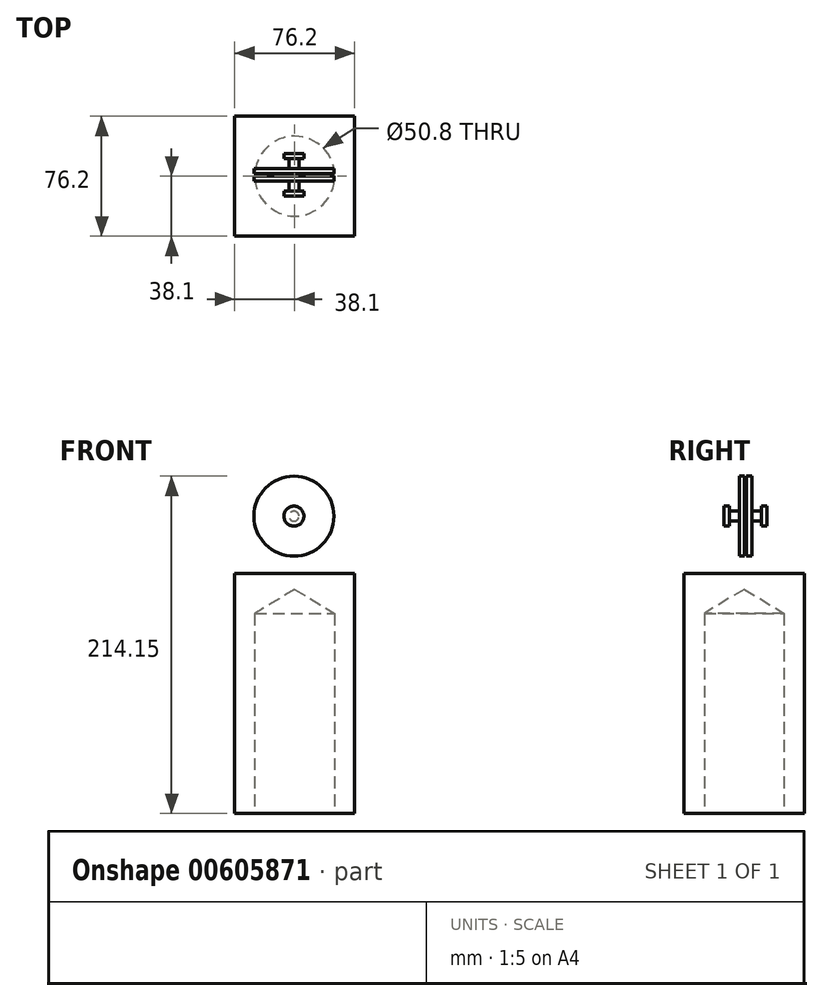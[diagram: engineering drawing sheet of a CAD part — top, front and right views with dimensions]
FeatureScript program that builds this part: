
annotation { "Feature Type Name" : "Feature", "Feature Type Description" : "" }
export const myFeature = defineFeature(function(context is Context, id is Id, definition is map)
    precondition{}
    {
        {
            var Q0;
            Q0=qCreatedBy(makeId("Front.planeOp"),FACE);
            var sketch = newSketch(context, id + "F0", { "sketchPlane" : qUnion([Q0])});
            skLineSegment(sketch, "E0", {"start": v(0, 0) * mm, "end": v(76.2, 0) * mm});
            skLineSegment(sketch, "E1", {"start": v(76.2, 0) * mm, "end": v(76.2, 152.4) * mm});
            skLineSegment(sketch, "E2", {"start": v(76.2, 152.4) * mm, "end": v(0, 152.4) * mm});
            skLineSegment(sketch, "E3", {"start": v(0, 152.4) * mm, "end": v(0, 0) * mm});
            skSolve(sketch);
        }
        {
            var Q0;
            Q0=makeQuery(id+"F0.imprint","IMPRINT",FACE,{"disambiguationData":[TD([[makeQuery(id+"F0.imprint","IMPRINT",EDGE,{"derivedFrom":sQuery(id+"F0.wireOp",EDGE,"E0")}),1.0]])]});
            extrude(context, id + "F1", {"entities" : qUnion([Q0]), "oppositeDirection" : true, "depth" : 76.2 * mm, "offsetDistance" : 25.4 * mm});
        }
        {
            var Q0;
            Q0=makeQuery(id+"F1.opExtrude","SWEPT_FACE",FACE,{"disambiguationData":[OSD([sQuery(id+"F0.wireOp",EDGE,"E0")])]});
            var sketch = newSketch(context, id + "F2", { "sketchPlane" : qUnion([Q0])});
            skLineSegment(sketch, "E4", {"start": v(76.2, -38.1) * mm, "end": v(38.1, -38.1) * mm});
            skPoint(sketch, "E4.endSnap0", {"position": v(76.2, -38.1) * mm});
            skSolve(sketch);
        }
        {
            var Q0;
            Q0=sQuery(id+"F2.wireOp",VERTEX,"E4.end");
            var Q1;
            Q1=makeQuery(id+"F1.opExtrude","SWEPT_BODY",BODY,{"disambiguationData":[OSD([sQuery(id+"F0.wireOp",EDGE,"E0"),sQuery(id+"F0.wireOp",EDGE,"E1"),sQuery(id+"F0.wireOp",EDGE,"E2"),sQuery(id+"F0.wireOp",EDGE,"E3")])]});
            hole(context, id + "F3", {"style" : HoleStyle.SIMPLE, "endStyle" : HoleEndStyle.BLIND, "holeDiameter" : 50.8 * mm, "majorDiameter" : 6.35 * mm, "holeDepth" : 127 * mm, "isTappedThrough" : true, "tappedDepth" : 12.7 * mm, "tapClearance" : 3, "startFromSketch" : true, "locations" : qUnion([Q0]), "scope" : qUnion([Q1])});
        }
        {
            var Q0;
            Q0=qCreatedBy(makeId("Front.planeOp"),FACE);
            cPlane(context, id + "F4", {"entities" : qUnion([Q0]), "cplaneType" : CPlaneType.OFFSET, "offset" : 38.1 * mm, "oppositeDirection" : true, "width" : 152.4 * mm, "height" : 152.4 * mm});
        }
        {
            var Q0;
            Q0=qCreatedBy(id+"F4.planeOp",FACE);
            var sketch = newSketch(context, id + "F5", { "sketchPlane" : qUnion([Q0])});
            skCircle(sketch, "E5", {"center": v(37.63, 188.75) * mm, "radius": 25.4 * mm});
            skSolve(sketch);
        }
        {
            var Q0;
            Q0=makeQuery(id+"F1.opExtrude","CAP_VERTEX",VERTEX,{"disambiguationData":[OSD([sQuery(id+"F0.wireOp",EDGE,"E2"),sQuery(id+"F0.wireOp",EDGE,"E3")])],"isStart":true});
            var Q1;
            Q1=makeQuery(id+"F1.opExtrude","CAP_VERTEX",VERTEX,{"disambiguationData":[OSD([sQuery(id+"F0.wireOp",EDGE,"E1"),sQuery(id+"F0.wireOp",EDGE,"E2")])],"isStart":true});
            var Q2;
            Q2=sQuery(id+"F5.wireOp",VERTEX,"E5.center");
            cPlane(context, id + "F6", {"entities" : qUnion([Q0, Q1, Q2]), "cplaneType" : CPlaneType.THREE_POINT, "offset" : 25.4 * mm, "width" : 152.4 * mm, "height" : 152.4 * mm});
        }
        {
            var Q0;
            Q0=makeQuery(id+"F5.imprint","IMPRINT",FACE,{"disambiguationData":[TD([[makeQuery(id+"F5.imprint","IMPRINT",EDGE,{"derivedFrom":sQuery(id+"F5.wireOp",EDGE,"E5")}),1.0]])]});
            extrude(context, id + "F7", {"entities" : qUnion([Q0]), "depth" : 3.17 * mm, "offsetDistance" : 25.4 * mm});
        }
        {
            var Q0;
            Q0=makeQuery(id+"F7.opExtrude","CAP_FACE",FACE,{"disambiguationData":[OSD([sQuery(id+"F5.wireOp",EDGE,"E5")])],"isStart":true});
            var sketch = newSketch(context, id + "F8", { "sketchPlane" : qUnion([Q0])});
            skCircle(sketch, "E6", {"center": v(-37.63, 188.75) * mm, "radius": 3.18 * mm});
            skSolve(sketch);
        }
        {
            var Q0;
            Q0=makeQuery(id+"F8.imprint","IMPRINT",FACE,{"disambiguationData":[TD([[makeQuery(id+"F8.imprint","IMPRINT",EDGE,{"derivedFrom":sQuery(id+"F8.wireOp",EDGE,"E6")}),1.0]])]});
            var Q1;
            Q1=sQuery(id+"F8.wireOp",EDGE,"E6");
            extrude(context, id + "F9", {"entities" : qUnion([Q0]), "operationType" : NewBodyOperationType.ADD, "surfaceEntities" : qUnion([Q1]), "depth" : 1.59 * mm, "offsetDistance" : 25.4 * mm});
        }
        {
            var Q0;
            Q0=makeQuery(id+"F9.opExtrude","CAP_FACE",FACE,{"disambiguationData":[OSD([sQuery(id+"F8.wireOp",EDGE,"E6")])],"isStart":false});
            var sketch = newSketch(context, id + "F10", { "sketchPlane" : qUnion([Q0])});
            skCircle(sketch, "E7", {"center": v(-37.63, 188.75) * mm, "radius": 25.4 * mm});
            skSolve(sketch);
        }
        {
            var Q0;
            Q0=makeQuery(id+"F10.imprint","IMPRINT",FACE,{"disambiguationData":[TD([[makeQuery(id+"F10.imprint","IMPRINT",EDGE,{"derivedFrom":makeQuery(id+"F9.opExtrude","CAP_EDGE",EDGE,{"disambiguationData":[OSD([sQuery(id+"F8.wireOp",EDGE,"E6")])],"isStart":false})}),1.0]])]});
            extrude(context, id + "F11", {"entities" : qUnion([Q0]), "operationType" : NewBodyOperationType.ADD, "depth" : 3.17 * mm, "offsetDistance" : 25.4 * mm});
        }
        {
            var Q0;
            Q0=makeQuery(id+"F10.imprint","IMPRINT",FACE,{"disambiguationData":[TD([[makeQuery(id+"F10.imprint","IMPRINT",EDGE,{"derivedFrom":sQuery(id+"F10.wireOp",EDGE,"E7")}),1.0]])]});
            extrude(context, id + "F12", {"entities" : qUnion([Q0]), "operationType" : NewBodyOperationType.ADD, "depth" : 3.17 * mm, "offsetDistance" : 25.4 * mm});
        }
        {
            var Q0;
            {var subQ0=sQuery(id+"F8.wireOp",EDGE,"E6");Q0=makeQuery(id+"F12.boolean.opBoolean","MERGE",FACE,{"derivedFrom":[makeQuery(id+"F11.opExtrude","CAP_FACE",FACE,{"disambiguationData":[OSD([subQ0])],"isStart":false}),makeQuery(id+"F12.opExtrude","CAP_FACE",FACE,{"disambiguationData":[OSD([subQ0,sQuery(id+"F10.wireOp",EDGE,"E7")])],"isStart":false})]});}
            var sketch = newSketch(context, id + "F13", { "sketchPlane" : qUnion([Q0])});
            skCircle(sketch, "E8", {"center": v(-37.63, 188.75) * mm, "radius": 3.18 * mm});
            skSolve(sketch);
        }
        {
            var Q0;
            Q0=makeQuery(id+"F13.imprint","IMPRINT",FACE,{"disambiguationData":[TD([[makeQuery(id+"F13.imprint","IMPRINT",EDGE,{"derivedFrom":sQuery(id+"F13.wireOp",EDGE,"E8")}),1.0]])]});
            extrude(context, id + "F14", {"entities" : qUnion([Q0]), "operationType" : NewBodyOperationType.ADD, "depth" : 6.35 * mm, "offsetDistance" : 25.4 * mm});
        }
        {
            var Q0;
            Q0=makeQuery(id+"F7.opExtrude","CAP_FACE",FACE,{"disambiguationData":[OSD([sQuery(id+"F5.wireOp",EDGE,"E5")])],"isStart":false});
            var sketch = newSketch(context, id + "F15", { "sketchPlane" : qUnion([Q0])});
            skCircle(sketch, "E9", {"center": v(37.63, 188.75) * mm, "radius": 3.18 * mm});
            skSolve(sketch);
        }
        {
            var Q0;
            Q0=makeQuery(id+"F15.imprint","IMPRINT",FACE,{"disambiguationData":[TD([[makeQuery(id+"F15.imprint","IMPRINT",EDGE,{"derivedFrom":sQuery(id+"F15.wireOp",EDGE,"E9")}),1.0]])]});
            extrude(context, id + "F16", {"entities" : qUnion([Q0]), "operationType" : NewBodyOperationType.ADD, "depth" : 6.35 * mm, "offsetDistance" : 25.4 * mm});
        }
        {
            var Q0;
            Q0=makeQuery(id+"F16.opExtrude","CAP_FACE",FACE,{"disambiguationData":[OSD([sQuery(id+"F15.wireOp",EDGE,"E9")])],"isStart":false});
            var sketch = newSketch(context, id + "F17", { "sketchPlane" : qUnion([Q0])});
            skCircle(sketch, "E10", {"center": v(37.63, 188.75) * mm, "radius": 6.35 * mm});
            skSolve(sketch);
        }
        {
            var Q0;
            Q0=makeQuery(id+"F17.imprint","IMPRINT",FACE,{"disambiguationData":[TD([[makeQuery(id+"F17.imprint","IMPRINT",EDGE,{"derivedFrom":makeQuery(id+"F16.opExtrude","CAP_EDGE",EDGE,{"disambiguationData":[OSD([sQuery(id+"F15.wireOp",EDGE,"E9")])],"isStart":false})}),1.0]])]});
            extrude(context, id + "F18", {"entities" : qUnion([Q0]), "operationType" : NewBodyOperationType.ADD, "depth" : 3.17 * mm, "offsetDistance" : 25.4 * mm});
        }
        {
            var Q0;
            Q0=makeQuery(id+"F17.imprint","IMPRINT",FACE,{"disambiguationData":[TD([[makeQuery(id+"F17.imprint","IMPRINT",EDGE,{"derivedFrom":sQuery(id+"F17.wireOp",EDGE,"E10")}),1.0]])]});
            extrude(context, id + "F19", {"entities" : qUnion([Q0]), "operationType" : NewBodyOperationType.ADD, "depth" : 3.17 * mm, "offsetDistance" : 25.4 * mm});
        }
        {
            var Q0;
            Q0=makeQuery(id+"F14.opExtrude","CAP_FACE",FACE,{"disambiguationData":[OSD([sQuery(id+"F13.wireOp",EDGE,"E8")])],"isStart":false});
            var sketch = newSketch(context, id + "F20", { "sketchPlane" : qUnion([Q0])});
            skCircle(sketch, "E11", {"center": v(-37.63, 188.75) * mm, "radius": 6.35 * mm});
            skSolve(sketch);
        }
        {
            var Q0;
            Q0=makeQuery(id+"F20.imprint","IMPRINT",FACE,{"disambiguationData":[TD([[makeQuery(id+"F20.imprint","IMPRINT",EDGE,{"derivedFrom":makeQuery(id+"F14.opExtrude","CAP_EDGE",EDGE,{"disambiguationData":[OSD([sQuery(id+"F13.wireOp",EDGE,"E8")])],"isStart":false})}),1.0]])]});
            extrude(context, id + "F21", {"entities" : qUnion([Q0]), "operationType" : NewBodyOperationType.ADD, "depth" : 3.17 * mm, "offsetDistance" : 25.4 * mm});
        }
        {
            var Q0;
            Q0 = qSketchRegion(id + "F20", true);
            extrude(context, id + "F22", {"entities" : qUnion([Q0]), "operationType" : NewBodyOperationType.ADD, "depth" : 3.17 * mm, "offsetDistance" : 25.4 * mm});
        }
        {
            var Q0;
            Q0=makeQuery(id+"F1.opExtrude","SWEPT_FACE",FACE,{"disambiguationData":[OSD([sQuery(id+"F0.wireOp",EDGE,"E0")])]});
            var sketch = newSketch(context, id + "F23", { "sketchPlane" : qUnion([Q0])});
            skCircle(sketch, "E12", {"center": v(38.1, -38.1) * mm, "radius": 25.4 * mm});
            skSolve(sketch);
        }
        {
            var Q0;
            Q0=sQuery(id+"F23.wireOp",EDGE,"E12");
            extrude(context, id + "F24", {"bodyType" : ToolBodyType.SURFACE, "surfaceEntities" : qUnion([Q0]), "depth" : 25.4 * mm, "offsetDistance" : 25.4 * mm});
        }
    });
